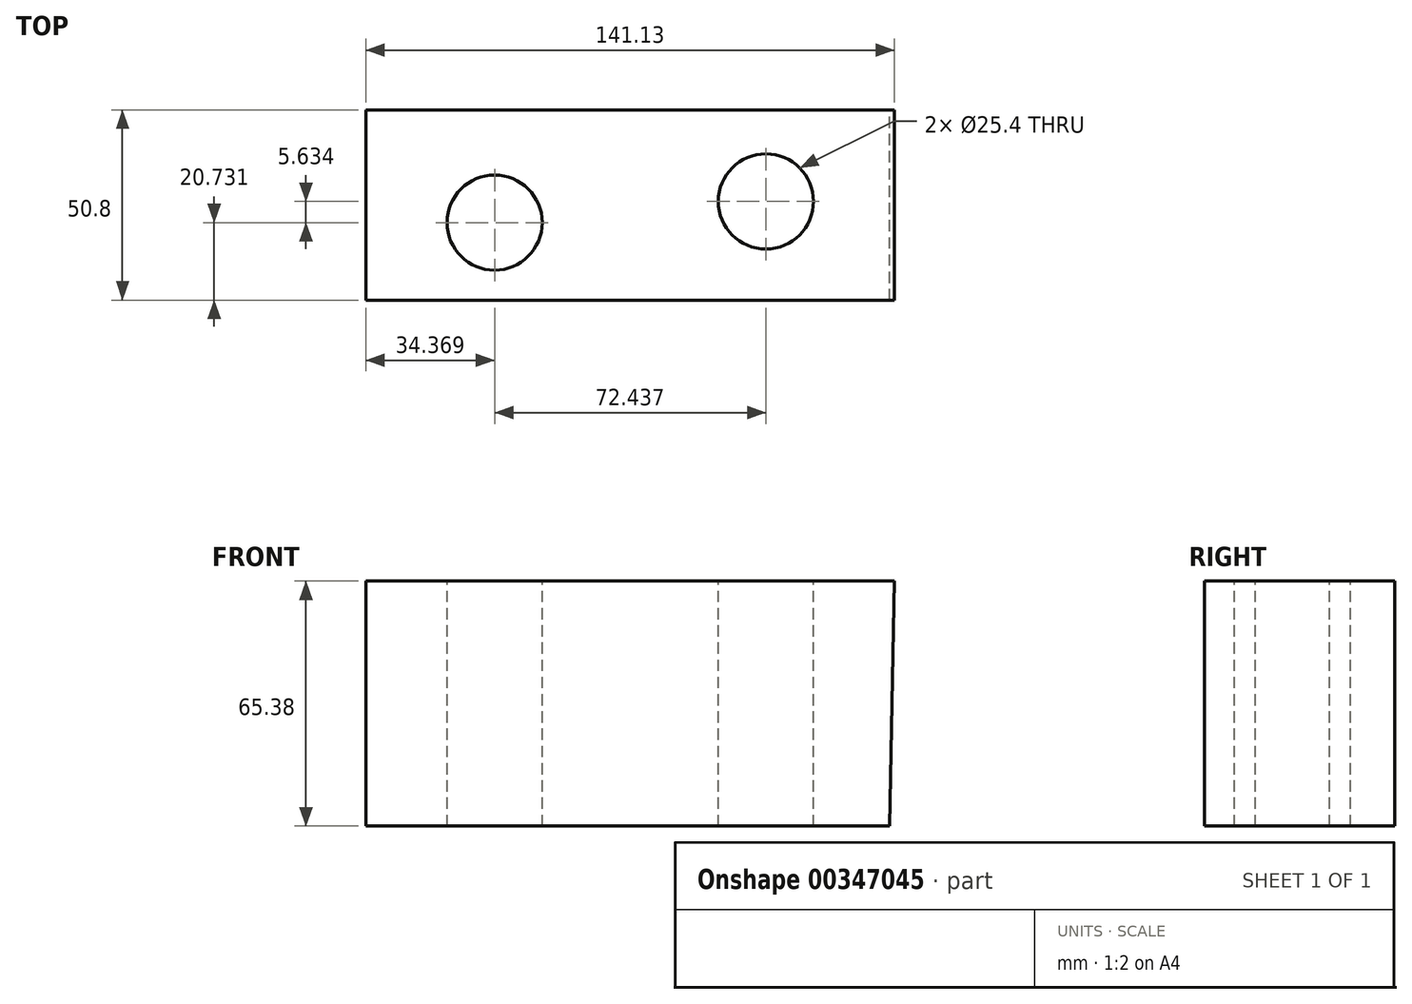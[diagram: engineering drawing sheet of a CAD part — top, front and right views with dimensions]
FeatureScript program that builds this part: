
annotation { "Feature Type Name" : "Feature", "Feature Type Description" : "" }
export const myFeature = defineFeature(function(context is Context, id is Id, definition is map)
    precondition{}
    {
        {
            var Q0;
            Q0=qCreatedBy(makeId("Front.planeOp"),FACE);
            var sketch = newSketch(context, id + "F0", { "sketchPlane" : qUnion([Q0])});
            skLineSegment(sketch, "E0", {"start": v(66.3, 0) * mm, "end": v(-73.58, 0) * mm});
            skLineSegment(sketch, "E1", {"start": v(-73.58, 0) * mm, "end": v(-73.58, 65.38) * mm});
            skLineSegment(sketch, "E2", {"start": v(-73.58, 65.38) * mm, "end": v(67.55, 65.38) * mm});
            skLineSegment(sketch, "E3", {"start": v(67.55, 65.38) * mm, "end": v(66.3, 0) * mm});
            skSolve(sketch);
        }
        {
            var Q0;
            Q0 = qSketchRegion(id + "F0", true);
            extrude(context, id + "F1", {"entities" : qUnion([Q0]), "depth" : 50.8 * mm});
        }
        {
            var Q0;
            Q0=makeQuery(id+"F1.opExtrude","SWEPT_FACE",FACE,{"disambiguationData":[OSD([sQuery(id+"F0.wireOp",EDGE,"E2")])]});
            var sketch = newSketch(context, id + "F2", { "sketchPlane" : qUnion([Q0])});
            skPoint(sketch, "E4", {"position": v(-39.21, -30.07) * mm});
            skPoint(sketch, "E5", {"position": v(35.36, -31.83) * mm});
            skSolve(sketch);
        }
        {
            var Q0;
            Q0=sQuery(id+"F2.wireOp",VERTEX,"E4");
            var Q1;
            Q1=makeQuery(id+"F1.opExtrude","SWEPT_BODY",BODY,{"disambiguationData":[OSD([sQuery(id+"F0.wireOp",EDGE,"E0"),sQuery(id+"F0.wireOp",EDGE,"E1"),sQuery(id+"F0.wireOp",EDGE,"E2"),sQuery(id+"F0.wireOp",EDGE,"E3")])]});
            hole(context, id + "F3", {"style" : HoleStyle.SIMPLE, "endStyle" : HoleEndStyle.THROUGH, "holeDiameter" : 25.4 * mm, "isTappedThrough" : true, "tappedDepth" : 12.7 * mm, "tapClearance" : 3, "locations" : qUnion([Q0]), "scope" : qUnion([Q1])});
        }
        {
            var Q0;
            Q0=makeQuery(id+"F1.opExtrude","SWEPT_FACE",FACE,{"disambiguationData":[OSD([sQuery(id+"F0.wireOp",EDGE,"E2")])]});
            var sketch = newSketch(context, id + "F4", { "sketchPlane" : qUnion([Q0])});
            skPoint(sketch, "E6", {"position": v(33.23, -24.44) * mm});
            skSolve(sketch);
        }
        {
            var Q0;
            Q0=sQuery(id+"F4.wireOp",VERTEX,"E6");
            var Q1;
            Q1=makeQuery(id+"F1.opExtrude","SWEPT_BODY",BODY,{"disambiguationData":[OSD([sQuery(id+"F0.wireOp",EDGE,"E0"),sQuery(id+"F0.wireOp",EDGE,"E1"),sQuery(id+"F0.wireOp",EDGE,"E2"),sQuery(id+"F0.wireOp",EDGE,"E3")])]});
            hole(context, id + "F5", {"style" : HoleStyle.SIMPLE, "endStyle" : HoleEndStyle.THROUGH, "holeDiameter" : 25.4 * mm, "isTappedThrough" : true, "tappedDepth" : 12.7 * mm, "tapClearance" : 3, "locations" : qUnion([Q0]), "scope" : qUnion([Q1])});
        }
    });
